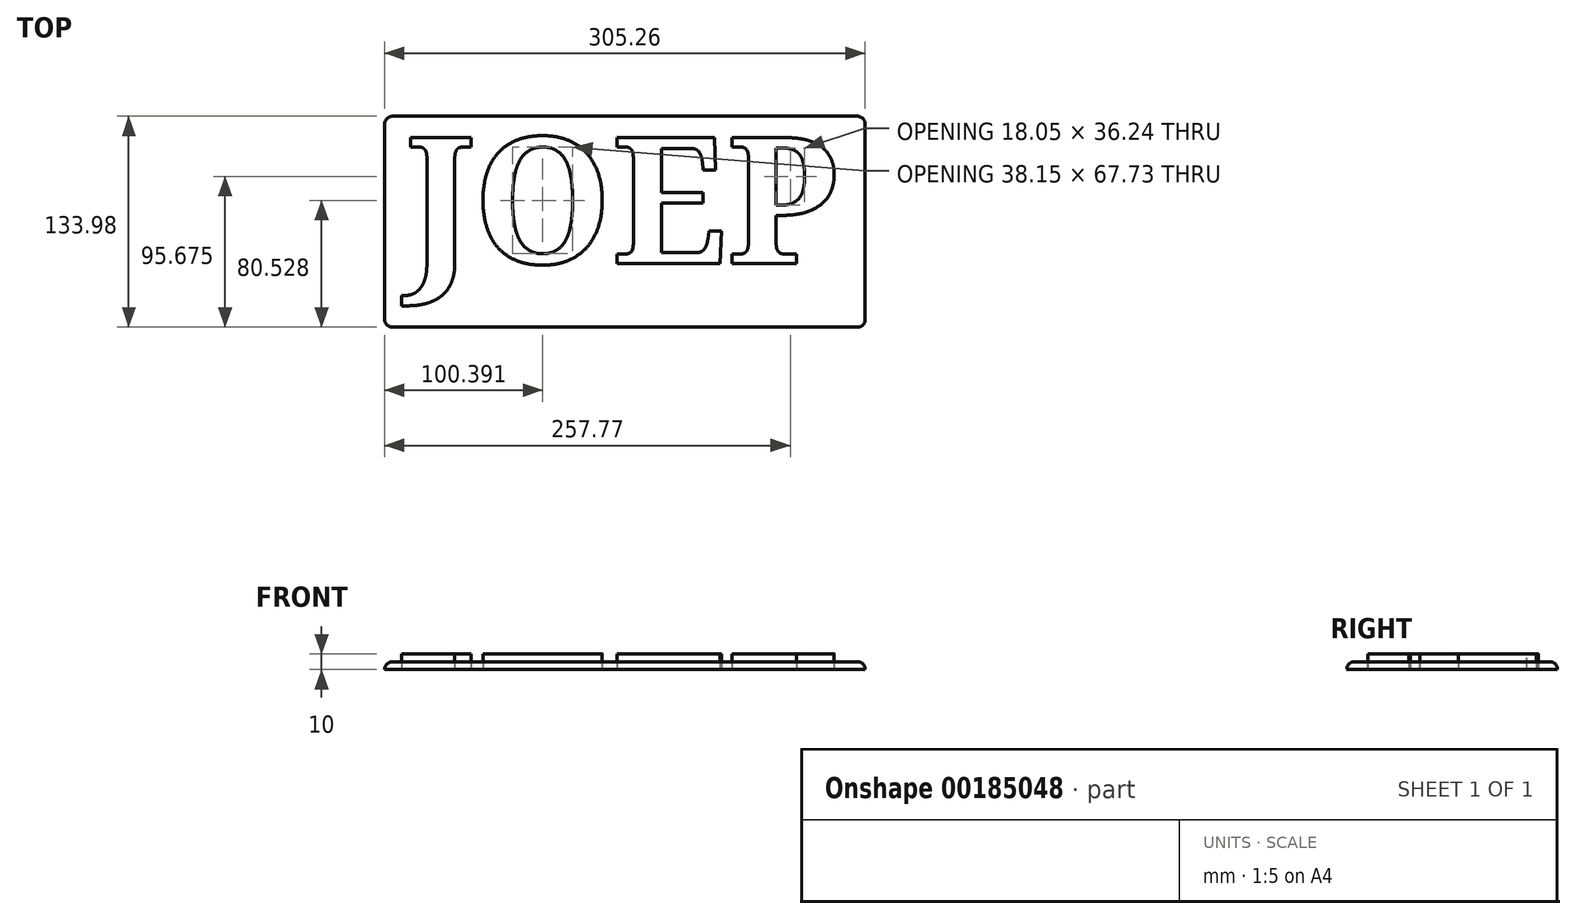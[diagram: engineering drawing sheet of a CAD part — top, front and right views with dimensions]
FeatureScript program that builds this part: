
annotation { "Feature Type Name" : "Feature", "Feature Type Description" : "" }
export const myFeature = defineFeature(function(context is Context, id is Id, definition is map)
    precondition{}
    {
        {
            var Q0;
            Q0=qCreatedBy(makeId("Top.planeOp"),FACE);
            var sketch = newSketch(context, id + "F0", { "sketchPlane" : qUnion([Q0])});
            skText(sketch, "E0", { "text": "JOEP", "fontName": "NotoSerif-Bold.ttf"});
            const initialGuessF0  = {"E0": [-0.15675, -0.0421, 1, 0, 0.0806]};
            skSetInitialGuess(sketch, initialGuessF0);
            skSolve(sketch);
        }
        {
            var Q0;
            Q0=makeQuery(id+"F0.imprint","IMPRINT",FACE,{"disambiguationData":[TD([[makeQuery(id+"F0.imprint","IMPRINT",EDGE,{"derivedFrom":sQuery(id+"F0.wireOp",EDGE,"E0.sketch_text.stroke-28")}),-1.0]])]});
            var Q1;
            Q1=makeQuery(id+"F0.imprint","IMPRINT",FACE,{"disambiguationData":[TD([[makeQuery(id+"F0.imprint","IMPRINT",EDGE,{"derivedFrom":sQuery(id+"F0.wireOp",EDGE,"E0.sketch_text.stroke-0")}),-1.0]])]});
            var Q2;
            Q2=makeQuery(id+"F0.imprint","IMPRINT",FACE,{"disambiguationData":[TD([[makeQuery(id+"F0.imprint","IMPRINT",EDGE,{"derivedFrom":sQuery(id+"F0.wireOp",EDGE,"E0.sketch_text.stroke-60")}),-1.0]])]});
            var Q3;
            Q3=makeQuery(id+"F0.imprint","IMPRINT",FACE,{"disambiguationData":[TD([[makeQuery(id+"F0.imprint","IMPRINT",EDGE,{"derivedFrom":sQuery(id+"F0.wireOp",EDGE,"E0.sketch_text.stroke-94")}),-1.0]])]});
            extrude(context, id + "F1", {"entities" : qUnion([Q0, Q1, Q2, Q3]), "depth" : 10 * mm});
        }
        {
            var Q0;
            Q0=qCreatedBy(makeId("Top.planeOp"),FACE);
            var sketch = newSketch(context, id + "F2", { "sketchPlane" : qUnion([Q0])});
            skLineSegment(sketch, "E1.bottom", {"start": v(-171.88, 51.39) * mm, "end": v(133.38, 51.39) * mm});
            skLineSegment(sketch, "E1.top", {"start": v(-171.88, -82.6) * mm, "end": v(133.38, -82.6) * mm});
            skLineSegment(sketch, "E1.left", {"start": v(-171.88, 51.39) * mm, "end": v(-171.88, -82.6) * mm});
            skLineSegment(sketch, "E1.right", {"start": v(133.38, 51.39) * mm, "end": v(133.38, -82.6) * mm});
            skSolve(sketch);
        }
        {
            var Q0;
            Q0=makeQuery(id+"F2.imprint","IMPRINT",FACE,{"disambiguationData":[TD([[makeQuery(id+"F2.imprint","IMPRINT",EDGE,{"derivedFrom":sQuery(id+"F2.wireOp",EDGE,"E1.bottom")}),-1.0]])]});
            extrude(context, id + "F3", {"entities" : qUnion([Q0]), "depth" : 5 * mm});
        }
        {
            var Q0;
            Q0=makeQuery(id+"F3.opExtrude","CAP_EDGE",EDGE,{"disambiguationData":[OSD([sQuery(id+"F2.wireOp",EDGE,"E1.bottom")])],"isStart":false});
            var Q1;
            Q1=makeQuery(id+"F3.opExtrude","CAP_EDGE",EDGE,{"disambiguationData":[OSD([sQuery(id+"F2.wireOp",EDGE,"E1.right")])],"isStart":false});
            var Q2;
            Q2=makeQuery(id+"F3.opExtrude","CAP_EDGE",EDGE,{"disambiguationData":[OSD([sQuery(id+"F2.wireOp",EDGE,"E1.top")])],"isStart":false});
            var Q3;
            Q3=makeQuery(id+"F3.opExtrude","CAP_EDGE",EDGE,{"disambiguationData":[OSD([sQuery(id+"F2.wireOp",EDGE,"E1.left")])],"isStart":false});
            var Q4;
            Q4=makeQuery(id+"F3.opExtrude","SWEPT_EDGE",EDGE,{"disambiguationData":[OSD([sQuery(id+"F2.wireOp",EDGE,"E1.top"),sQuery(id+"F2.wireOp",EDGE,"E1.left")])]});
            var Q5;
            Q5=makeQuery(id+"F3.opExtrude","SWEPT_EDGE",EDGE,{"disambiguationData":[OSD([sQuery(id+"F2.wireOp",EDGE,"E1.bottom"),sQuery(id+"F2.wireOp",EDGE,"E1.left")])]});
            var Q6;
            Q6=makeQuery(id+"F3.opExtrude","SWEPT_EDGE",EDGE,{"disambiguationData":[OSD([sQuery(id+"F2.wireOp",EDGE,"E1.bottom"),sQuery(id+"F2.wireOp",EDGE,"E1.right")])]});
            var Q7;
            Q7=makeQuery(id+"F3.opExtrude","SWEPT_EDGE",EDGE,{"disambiguationData":[OSD([sQuery(id+"F2.wireOp",EDGE,"E1.top"),sQuery(id+"F2.wireOp",EDGE,"E1.right")])]});
            fillet(context, id + "F4", {"entities" : qUnion([Q0, Q1, Q2, Q3, Q4, Q5, Q6, Q7]), "radius" : 5 * mm, "tangentPropagation" : true, "allowEdgeOverflow" : false});
        }
    });
